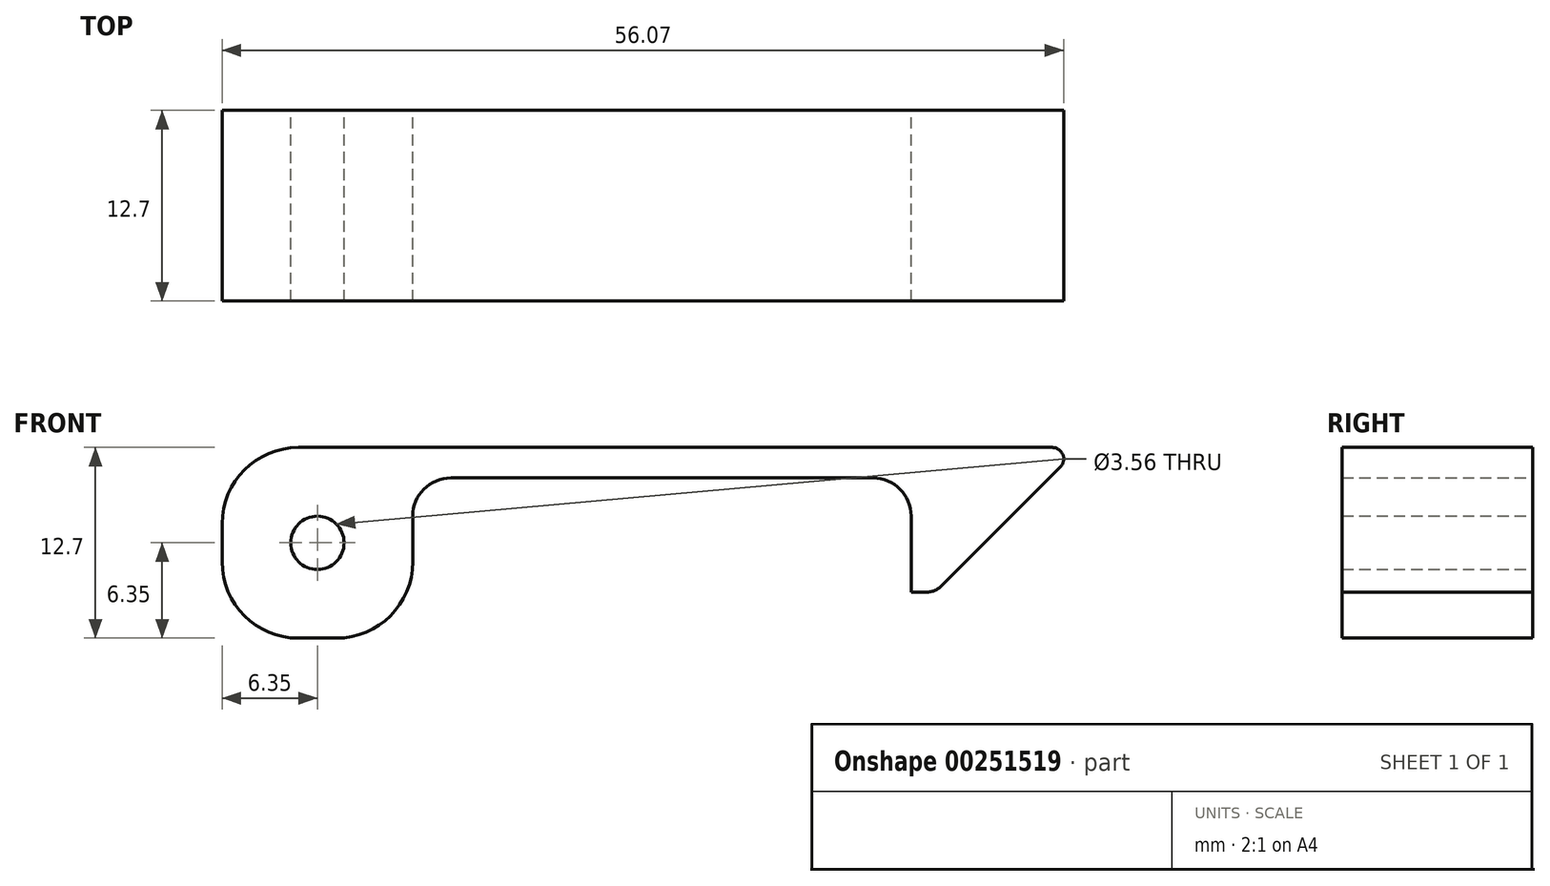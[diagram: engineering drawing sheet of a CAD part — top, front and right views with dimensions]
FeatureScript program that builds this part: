
annotation { "Feature Type Name" : "Feature", "Feature Type Description" : "" }
export const myFeature = defineFeature(function(context is Context, id is Id, definition is map)
    precondition{}
    {
        {
            var Q0;
            Q0=qCreatedBy(makeId("Front.planeOp"),FACE);
            var sketch = newSketch(context, id + "F0", { "sketchPlane" : qUnion([Q0])});
            skLineSegment(sketch, "E0", {"start": v(0, 0) * mm, "end": v(0, -12.7) * mm});
            skLineSegment(sketch, "E1", {"start": v(0, -12.7) * mm, "end": v(12.7, -12.7) * mm});
            skLineSegment(sketch, "E2", {"start": v(12.7, -12.7) * mm, "end": v(12.7, -4.57) * mm});
            skLineSegment(sketch, "E3", {"start": v(15.24, -2.03) * mm, "end": v(43.37, -2.03) * mm});
            skLineSegment(sketch, "E4", {"start": v(45.91, -4.57) * mm, "end": v(45.91, -9.65) * mm});
            skLineSegment(sketch, "E5", {"start": v(45.91, -9.65) * mm, "end": v(47.5, -9.65) * mm});
            skLineSegment(sketch, "E6", {"start": v(47.5, -9.65) * mm, "end": v(57.15, 0) * mm});
            skLineSegment(sketch, "E7", {"start": v(57.15, 0) * mm, "end": v(0, 0) * mm});
            skPoint(sketch, "E8.visualSharp", {"position": v(45.91, -2.03) * mm});
            skArc(sketch, "E8.filletArc", {"start": v(45.91, -4.57) * mm, "mid": v(45.17, -2.78) * mm, "end": v(43.37, -2.03) * mm});
            skPoint(sketch, "E9.visualSharp", {"position": v(12.7, -2.03) * mm});
            skArc(sketch, "E9.filletArc", {"start": v(15.24, -2.03) * mm, "mid": v(13.44, -2.78) * mm, "end": v(12.7, -4.57) * mm});
            skLineSegment(sketch, "E10", {"start": v(0, -6.35) * mm, "end": v(6.35, -6.35) * mm, "construction": true});
            skCircle(sketch, "E11", {"center": v(6.35, -6.35) * mm, "radius": 1.78 * mm});
            skSolve(sketch);
        }
        {
            var Q0;
            Q0 = qSketchRegion(id + "F0", true);
            extrude(context, id + "F1", {"entities" : qUnion([Q0]), "depth" : 12.7 * mm});
        }
        {
            var Q0;
            Q0=makeQuery(id+"F1.opExtrude","SWEPT_EDGE",EDGE,{"disambiguationData":[OSD([sQuery(id+"F0.wireOp",EDGE,"E5"),sQuery(id+"F0.wireOp",EDGE,"E6")])]});
            fillet(context, id + "F2", {"entities" : qUnion([Q0]), "radius" : 1.59 * mm, "tangentPropagation" : true, "allowEdgeOverflow" : false});
        }
        {
            var Q0;
            Q0=makeQuery(id+"F1.opExtrude","SWEPT_EDGE",EDGE,{"disambiguationData":[OSD([sQuery(id+"F0.wireOp",EDGE,"E6"),sQuery(id+"F0.wireOp",EDGE,"E7")])]});
            fillet(context, id + "F3", {"entities" : qUnion([Q0]), "radius" : 0.76 * mm, "tangentPropagation" : true, "allowEdgeOverflow" : false});
        }
        {
            var Q0;
            Q0=makeQuery(id+"F1.opExtrude","SWEPT_EDGE",EDGE,{"disambiguationData":[OSD([sQuery(id+"F0.wireOp",EDGE,"E0"),sQuery(id+"F0.wireOp",EDGE,"E1")])]});
            var Q1;
            Q1=makeQuery(id+"F1.opExtrude","SWEPT_EDGE",EDGE,{"disambiguationData":[OSD([sQuery(id+"F0.wireOp",EDGE,"E1"),sQuery(id+"F0.wireOp",EDGE,"E2")])]});
            var Q2;
            Q2=makeQuery(id+"F1.opExtrude","SWEPT_EDGE",EDGE,{"disambiguationData":[OSD([sQuery(id+"F0.wireOp",EDGE,"E0"),sQuery(id+"F0.wireOp",EDGE,"E7")])]});
            fillet(context, id + "F4", {"entities" : qUnion([Q0, Q1, Q2]), "radius" : 5.08 * mm, "tangentPropagation" : true, "allowEdgeOverflow" : false});
        }
    });
